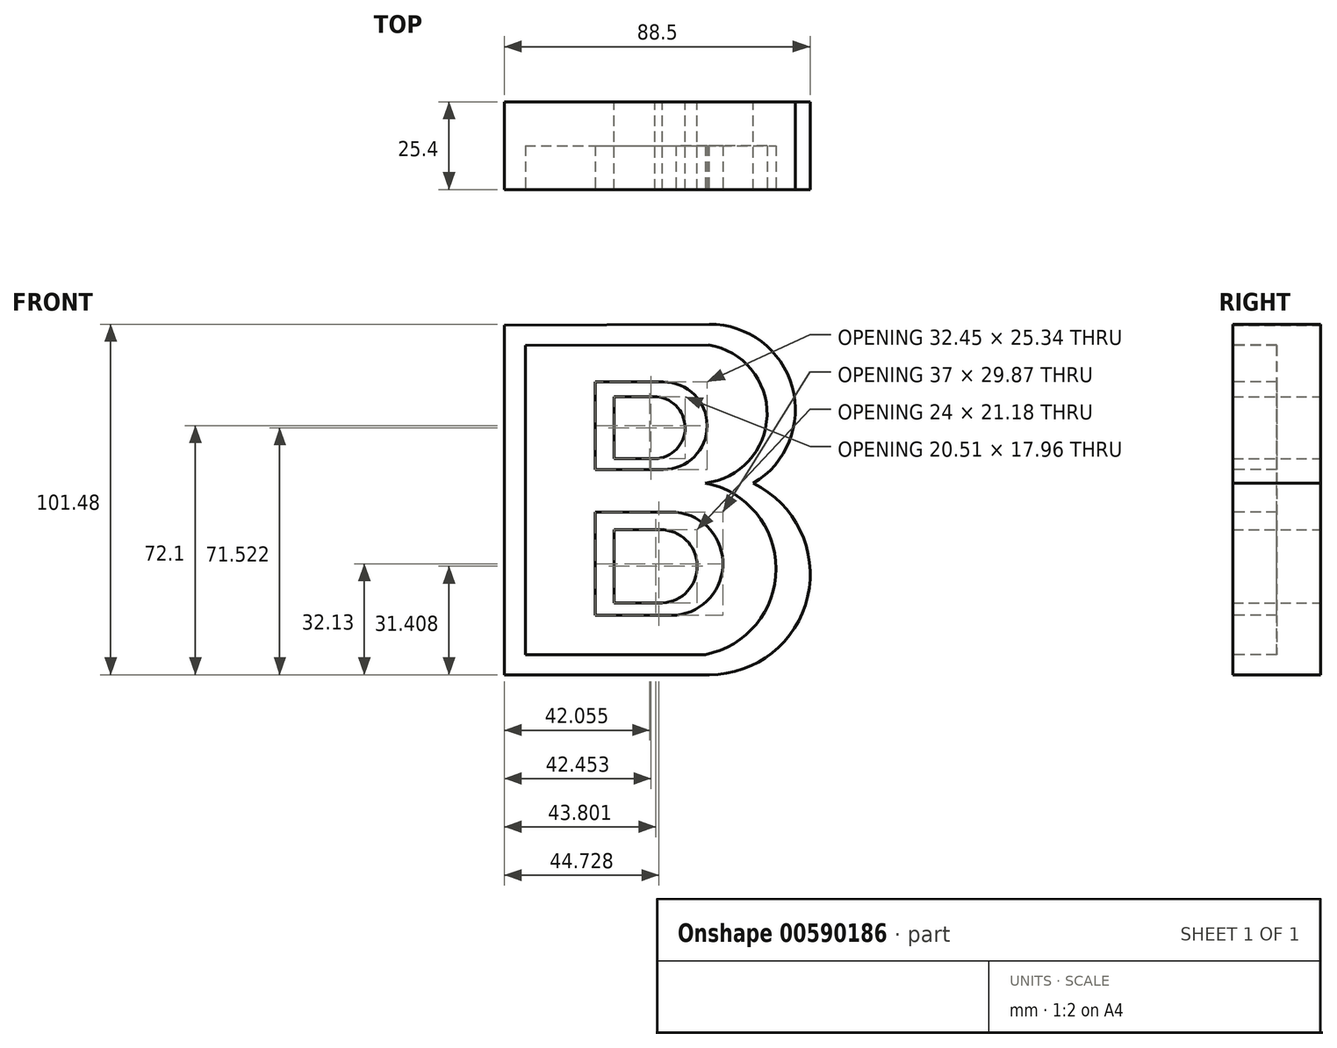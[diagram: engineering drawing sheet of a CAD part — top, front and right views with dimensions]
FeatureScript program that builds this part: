
annotation { "Feature Type Name" : "Feature", "Feature Type Description" : "" }
export const myFeature = defineFeature(function(context is Context, id is Id, definition is map)
    precondition{}
    {
        {
            var Q0;
            Q0=qCreatedBy(makeId("Front.planeOp"),FACE);
            var sketch = newSketch(context, id + "F0", { "sketchPlane" : qUnion([Q0])});
            skLineSegment(sketch, "E0", {"start": v(-89.9, 48.4) * mm, "end": v(-89.9, -52.82) * mm});
            skLineSegment(sketch, "E1", {"start": v(-89.9, -52.82) * mm, "end": v(-30.57, -52.82) * mm});
            skLineSegment(sketch, "E2", {"start": v(-30.57, 48.66) * mm, "end": v(-89.9, 48.4) * mm});
            skArc(sketch, "E3", {"start": v(-17.82, 2.6) * mm, "mid": v(-6.6, 30.5) * mm, "end": v(-30.57, 48.66) * mm});
            skArc(sketch, "E4", {"start": v(-30.57, -52.82) * mm, "mid": v(-2.14, -30.18) * mm, "end": v(-17.82, 2.6) * mm});
            skSolve(sketch);
        }
        {
            var Q0;
            Q0=qSketchRegion(id+"F0",true);
            extrude(context, id + "F1", {"entities" : qUnion([Q0]), "depth" : 25.4 * mm, "offsetDistance" : 25.4 * mm});
        }
        {
            var Q0;
            Q0=makeQuery(id+"F0.imprint","IMPRINT",FACE,{"disambiguationData":[TD([[makeQuery(id+"F0.imprint","IMPRINT",EDGE,{"derivedFrom":sQuery(id+"F0.wireOp",EDGE,"E0")}),1.0]])]});
            var sketch = newSketch(context, id + "F2", { "sketchPlane" : qUnion([Q0])});
            skLineSegment(sketch, "E5", {"start": v(-58.1, 27.68) * mm, "end": v(-58.1, 9.72) * mm});
            skLineSegment(sketch, "E6", {"start": v(-58.1, 27.68) * mm, "end": v(-46.57, 27.68) * mm});
            skLineSegment(sketch, "E7", {"start": v(-58.1, 9.72) * mm, "end": v(-46.38, 9.72) * mm});
            skLineSegment(sketch, "E8", {"start": v(-58.1, -10.82) * mm, "end": v(-58.1, -32) * mm});
            skLineSegment(sketch, "E9", {"start": v(-58.1, -32) * mm, "end": v(-44.13, -32) * mm});
            skLineSegment(sketch, "E10", {"start": v(-58.1, -10.82) * mm, "end": v(-44.7, -10.82) * mm});
            skArc(sketch, "E11", {"start": v(-46.38, 9.72) * mm, "mid": v(-37.6, 18.8) * mm, "end": v(-46.57, 27.68) * mm});
            skArc(sketch, "E12", {"start": v(-44.13, -32) * mm, "mid": v(-34.1, -21.14) * mm, "end": v(-44.7, -10.82) * mm});
            skSolve(sketch);
        }
        {
            var Q0;
            Q0=qSketchRegion(id+"F2",true);
            extrude(context, id + "F3", {"entities" : qUnion([Q0]), "operationType" : NewBodyOperationType.REMOVE, "oppositeDirection" : true, "depth" : 25.4 * mm, "offsetDistance" : 25.4 * mm});
        }
        {
            var Q0;
            Q0=qSketchRegion(id+"F2",true);
            extrude(context, id + "F4", {"entities" : qUnion([Q0]), "operationType" : NewBodyOperationType.REMOVE, "depth" : 53.85 * mm, "offsetDistance" : 25.4 * mm});
        }
        {
            var Q0;
            Q0=makeQuery(id+"F1.opExtrude","CAP_FACE",FACE,{"disambiguationData":[OSD([sQuery(id+"F0.wireOp",EDGE,"E0"),sQuery(id+"F0.wireOp",EDGE,"E1"),sQuery(id+"F0.wireOp",EDGE,"E2"),sQuery(id+"F0.wireOp",EDGE,"E3"),sQuery(id+"F0.wireOp",EDGE,"E4")])],"isStart":false});
            var sketch = newSketch(context, id + "F5", { "sketchPlane" : qUnion([Q0])});
            skLineSegment(sketch, "E13", {"start": v(-83.86, 42.46) * mm, "end": v(-83.86, -46.96) * mm});
            skLineSegment(sketch, "E14", {"start": v(-83.86, -46.96) * mm, "end": v(-31.74, -46.96) * mm});
            skLineSegment(sketch, "E15", {"start": v(-83.86, 42.46) * mm, "end": v(-30.7, 42.7) * mm});
            skLineSegment(sketch, "E16", {"start": v(-63.67, 31.95) * mm, "end": v(-63.67, 6.6) * mm});
            skLineSegment(sketch, "E17", {"start": v(-63.67, 6.6) * mm, "end": v(-43.9, 6.6) * mm});
            skLineSegment(sketch, "E18", {"start": v(-63.67, -35.63) * mm, "end": v(-63.67, -5.75) * mm});
            skLineSegment(sketch, "E19", {"start": v(-63.67, -5.75) * mm, "end": v(-40.18, -5.75) * mm});
            skLineSegment(sketch, "E20", {"start": v(-63.67, -35.63) * mm, "end": v(-41.63, -35.63) * mm});
            skLineSegment(sketch, "E21", {"start": v(-63.67, 31.95) * mm, "end": v(-43.9, 31.95) * mm});
            skArc(sketch, "E22", {"start": v(-43.9, 6.6) * mm, "mid": v(-31.22, 19.28) * mm, "end": v(-43.9, 31.95) * mm});
            skArc(sketch, "E23", {"start": v(-41.63, -35.63) * mm, "mid": v(-26.67, -21.38) * mm, "end": v(-40.18, -5.75) * mm});
            skArc(sketch, "E24", {"start": v(-31.74, -46.96) * mm, "mid": v(-11.25, -22.13) * mm, "end": v(-31.74, 2.7) * mm});
            skArc(sketch, "E25", {"start": v(-31.74, 2.7) * mm, "mid": v(-13.89, 22.25) * mm, "end": v(-30.7, 42.7) * mm});
            skSolve(sketch);
        }
        {
            var Q0;
            Q0=qSketchRegion(id+"F5",true);
            extrude(context, id + "F6", {"entities" : qUnion([Q0]), "oppositeDirection" : true, "depth" : 12.7 * mm, "offsetDistance" : 25.4 * mm});
        }
    });
